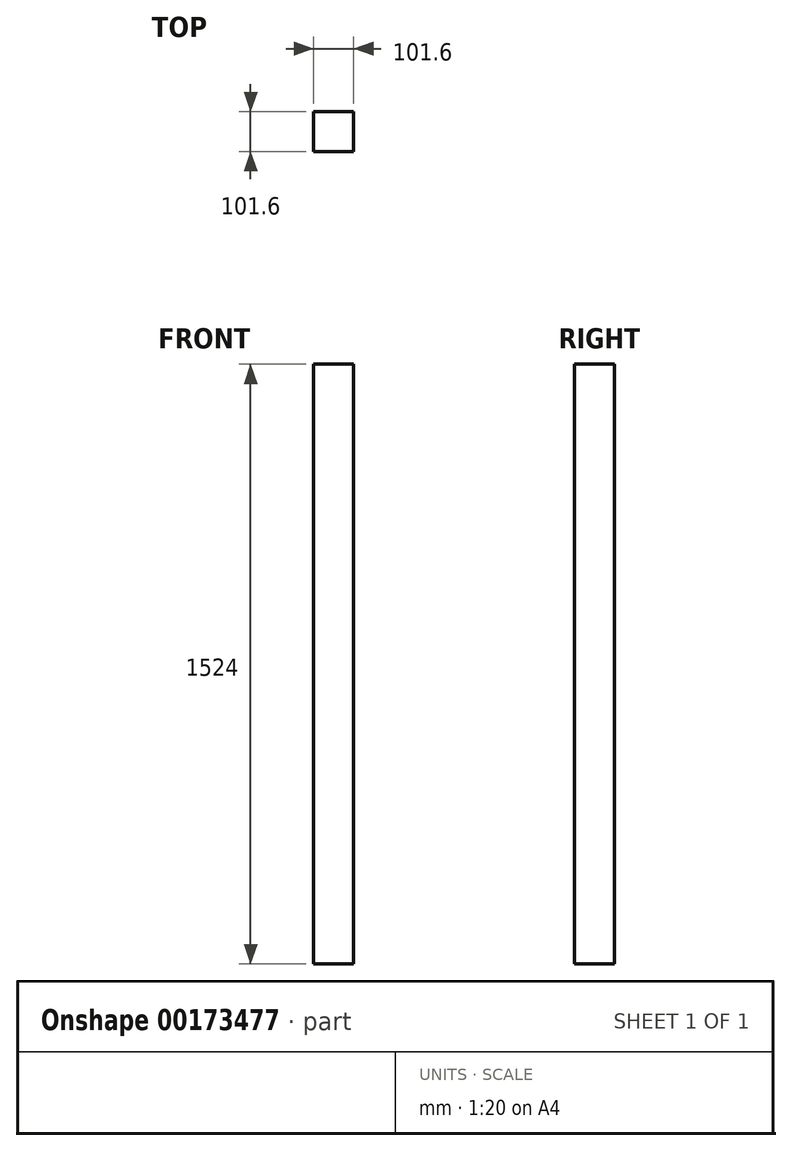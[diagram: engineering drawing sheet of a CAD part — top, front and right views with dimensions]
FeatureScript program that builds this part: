
annotation { "Feature Type Name" : "Feature", "Feature Type Description" : "" }
export const myFeature = defineFeature(function(context is Context, id is Id, definition is map)
    precondition{}
    {
        {
            var Q0;
            Q0=qCreatedBy(makeId("Top.planeOp"),FACE);
            var sketch = newSketch(context, id + "F0", { "sketchPlane" : qUnion([Q0])});
            skLineSegment(sketch, "E0.bottom", {"start": v(50.8, 50.8) * mm, "end": v(-50.8, 50.8) * mm});
            skLineSegment(sketch, "E0.top", {"start": v(50.8, -50.8) * mm, "end": v(-50.8, -50.8) * mm});
            skLineSegment(sketch, "E0.left", {"start": v(50.8, 50.8) * mm, "end": v(50.8, -50.8) * mm});
            skLineSegment(sketch, "E0.right", {"start": v(-50.8, 50.8) * mm, "end": v(-50.8, -50.8) * mm});
            skPoint(sketch, "E0.middle", {"position": v(0, 0) * mm});
            skSolve(sketch);
        }
        {
            var Q0;
            Q0 = qSketchRegion(id + "F0", true);
            extrude(context, id + "F1", {"entities" : qUnion([Q0]), "depth" : 1524 * mm});
        }
    });
